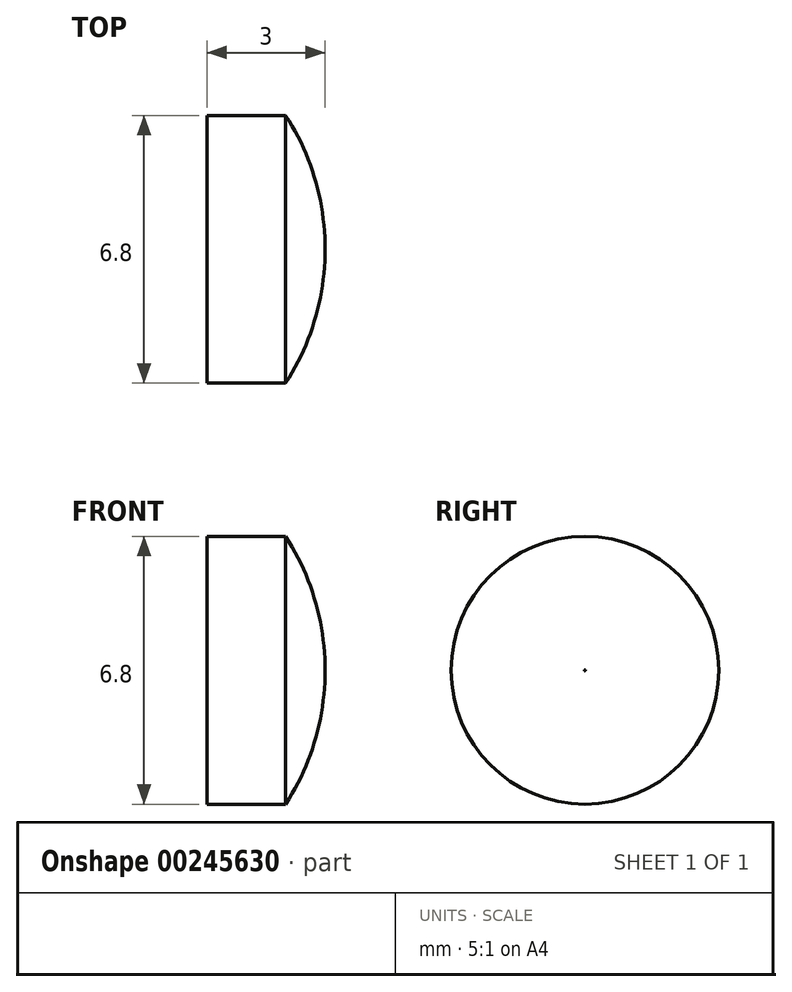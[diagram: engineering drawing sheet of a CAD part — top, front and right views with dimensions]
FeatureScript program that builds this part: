
annotation { "Feature Type Name" : "Feature", "Feature Type Description" : "" }
export const myFeature = defineFeature(function(context is Context, id is Id, definition is map)
    precondition{}
    {
        {
            var Q0;
            Q0=qCreatedBy(makeId("Front.planeOp"),FACE);
            var sketch = newSketch(context, id + "F0", { "sketchPlane" : qUnion([Q0])});
            skLineSegment(sketch, "E0", {"start": v(0, 0) * mm, "end": v(3, 0) * mm});
            skLineSegment(sketch, "E1", {"start": v(0, 0) * mm, "end": v(0, 3.4) * mm});
            skLineSegment(sketch, "E2", {"start": v(0, 3.4) * mm, "end": v(2, 3.4) * mm});
            skArc(sketch, "E3", {"start": v(3, 0) * mm, "mid": v(2.74, 1.77) * mm, "end": v(2, 3.4) * mm});
            skSolve(sketch);
        }
        {
            var Q0;
            Q0=makeQuery(id+"F0.imprint","IMPRINT",FACE,{"disambiguationData":[TD([[makeQuery(id+"F0.imprint","IMPRINT",EDGE,{"derivedFrom":sQuery(id+"F0.wireOp",EDGE,"E0")}),1.0]])]});
            var Q1;
            Q1=sQuery(id+"F0.wireOp",EDGE,"E0");
            revolve(context, id + "F1", {"entities" : qUnion([Q0]), "axis" : qUnion([Q1]), "revolveType" : RevolveType.FULL});
        }
    });
